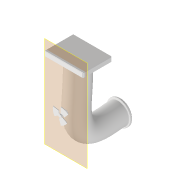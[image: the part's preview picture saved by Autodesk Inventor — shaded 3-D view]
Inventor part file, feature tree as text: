
AUTODESK INVENTOR PART (.ipt)
format: ipt  version: 2020 (Build 240168000, 168)  size: 673,280 bytes
history: native  units: mm
features: sketch x9, extrude x6, chamfer x3, fillet x2, sweep x1, plane x1, revolve x1, pattern_circular x1
ambient origin geometry x8: Origin, YZ Plane, XZ Plane, XY Plane, X Axis, Y Axis, Z Axis, Center Point
bodies: Volumenkörper1 (feature_tree)
feature tree (24):
  sweep  "Sweeping1"
  extrude  "Extrusion1"  Depth=10.0mm TaperAngle=0.0deg
  extrude  "Extrusion2"  Depth=300.0mm
  chamfer  "Fase1"  Distance=50.0mm
  chamfer  "Fase2"  Distance=5.0mm Angle=45.0deg
  fillet  "Rundung1"  Radius=2.0mm
  plane  "Arbeitsebene1"
  extrude  "Extrusion3"  Depth=4.769mm TaperAngle=0.0deg
  extrude  "Extrusion4"  Depth=40.0mm TaperAngle=0.0deg
  extrude  "Extrusion5"  Depth=20.0mm TaperAngle=0.0deg
  revolve  "Umdrehung1"
  fillet  "Rundung2"  Radius=60.0mm
  pattern_circular  "Runde Anordnung1"  [2 undecoded]
  extrude  "Extrusion6"  Depth=20.0mm
  chamfer  "Fase3"  Distance=30.0mm Angle=360.0deg
  sketch  "Skizze1"  dims[d0=200.0mm d1=220.0mm]
  sketch  "Skizze2"  dims[d2=0.0mm d3=0.0mm d4=10.0mm d5=0.0mm]
  sketch  "Skizze3"  dims[d6=400.0mm d7=300.0mm d8=50.0mm d9=0.0mm d10=5.0mm d11=2.0mm d12=45.0deg]
  sketch  "Skizze4"  dims[d13=10.0mm d14=2.0mm d15=45.0deg d16=2.0mm]
  sketch  "Skizze5"  dims[d17=50.0mm d18=4.769mm d19=0.0mm]
  sketch  "Skizze6"  dims[d20=15.0mm d21=40.0mm d22=0.0mm]
  sketch  "Skizze7"  dims[d23=30.0mm d24=20.0mm d25=0.0mm d26=60.0mm]
  sketch  "Skizze8"  dims[d27=5.0mm]
  sketch  "Skizze9"  dims[d28=5.0mm d29=6.981317mm d30=5.0mm d31=30.0mm d32=360.0deg d34=250.0mm d35=20.0mm d36=0.0mm d37=4.0mm d38=2.0mm d39=45.0deg d40=30.0mm d41=15.0mm]
note: 2 required parameter values undecoded (feature->parameter linkage not recoverable at this tier; creation-order binding heuristic only, values carry confidence <= 0.55)
